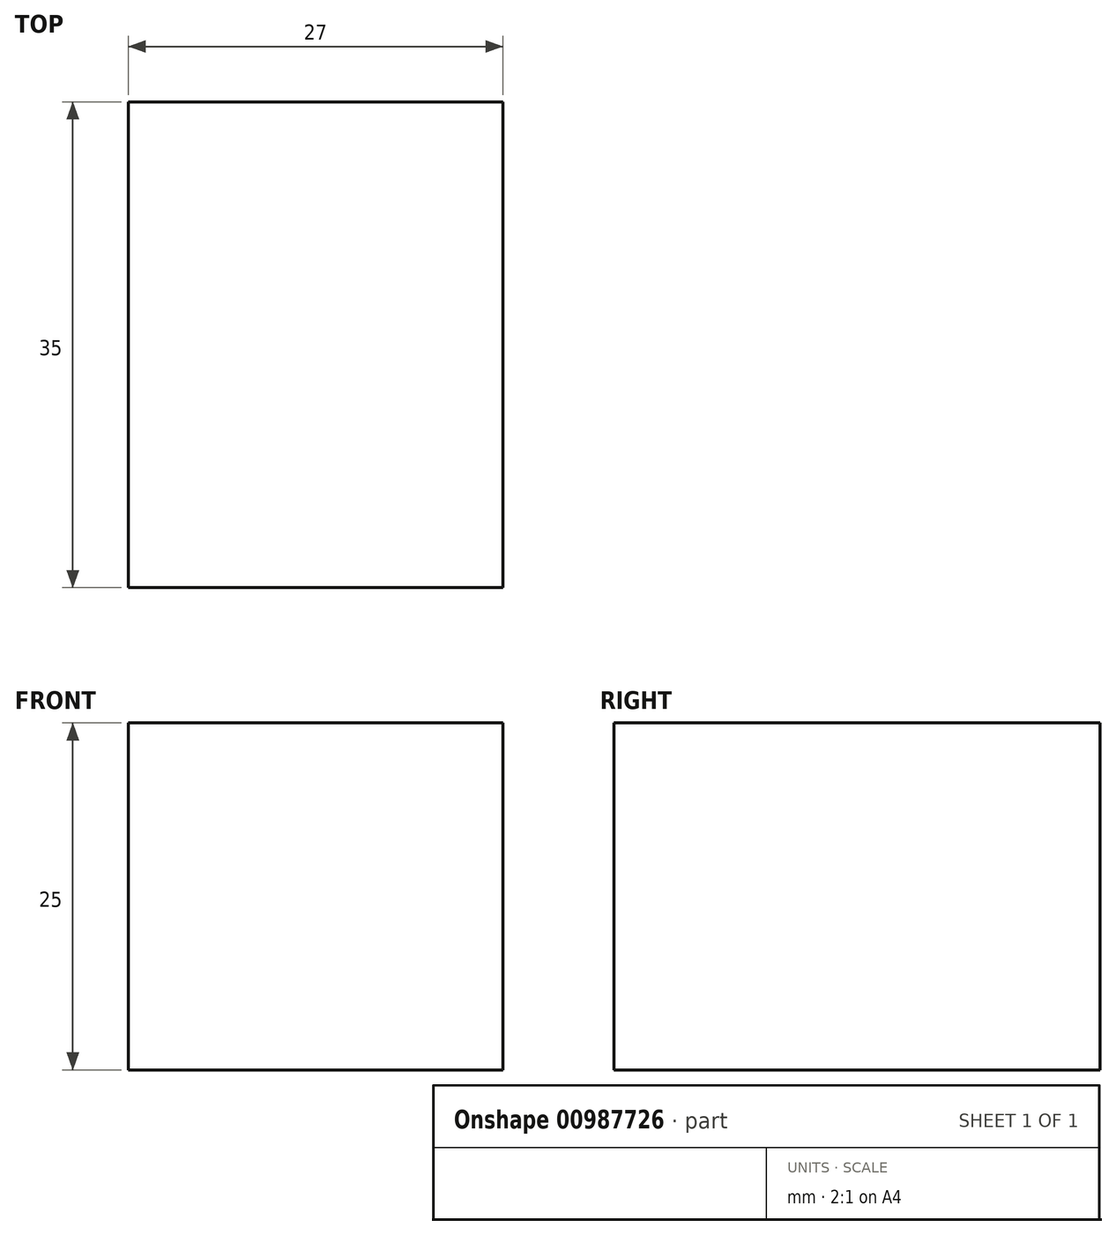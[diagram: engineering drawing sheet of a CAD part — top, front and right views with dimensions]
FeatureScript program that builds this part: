
annotation { "Feature Type Name" : "Feature", "Feature Type Description" : "" }
export const myFeature = defineFeature(function(context is Context, id is Id, definition is map)
    precondition{}
    {
        {
            var Q0;
            Q0=qCreatedBy(makeId("Top.planeOp"),FACE);
            var sketch = newSketch(context, id + "F0", { "sketchPlane" : qUnion([Q0])});
            skLineSegment(sketch, "E0.bottom", {"start": v(-13.5, 17.5) * mm, "end": v(13.5, 17.5) * mm});
            skLineSegment(sketch, "E0.top", {"start": v(-13.5, -17.5) * mm, "end": v(13.5, -17.5) * mm});
            skLineSegment(sketch, "E0.left", {"start": v(-13.5, 17.5) * mm, "end": v(-13.5, -17.5) * mm});
            skLineSegment(sketch, "E0.right", {"start": v(13.5, 17.5) * mm, "end": v(13.5, -17.5) * mm});
            skPoint(sketch, "E0.middle", {"position": v(0, 0) * mm});
            skSolve(sketch);
        }
        {
            var Q0;
            Q0 = qSketchRegion(id + "F0", true);
            extrude(context, id + "F1", {"entities" : qUnion([Q0]), "endBound" : BoundingType.SYMMETRIC, "depth" : 25 * mm, "offsetDistance" : 25 * mm});
        }
    });
